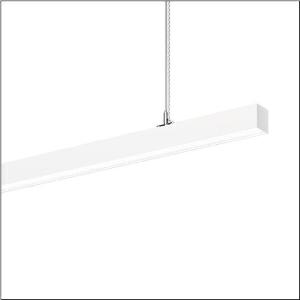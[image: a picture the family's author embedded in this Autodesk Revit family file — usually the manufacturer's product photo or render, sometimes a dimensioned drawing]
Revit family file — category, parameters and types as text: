
# Revit family: silica_r__21_51mx30dc49wb_27b8
name_source: partatom
category: Lighting Fixtures
units: mm (PartAtom-declared; Revit-internal decimal feet)

## family parameters
Cut with Voids When Loaded = No
Host = Face
Light Source = No
Part Type = Normal
Room Calculation Point = No
Round Connector Dimension = Use Diameter
Shared = No

## types (1)
- --- (1 x LED, 10520 lm, 64.1 W, 4000K)
    Apparent Load = 64 VA
    CIE Flux Codes = 47 79 96 57 100
    Color Rendering = 80
    Color Temperature = 4000K
    Default Elevation = 1800 mm
    Description = Silica® 21, office luminaire, primary optical cover: cover, of PMMA, opal, light emission: direct/indirect distribution, primary light characteristic: symmetric, installation type: suspended mounting, LED, rated luminous flux: 10.520lm, luminous efficacy: 164lm/W, light colour: 840, colour temperature: 4000K, with terminal, 3+2-pole, max. 2.5mm², mains connection: 220..240V, AC, 50/60Hz, rated input power: 64.1W, luminaire housing, of aluminium, traffic white (RAL 9016), length: 3.004mm, width: 53mm, height: 53mm, protection rating (complete): IP20, insulation class (complete): insulation class I (protective earthing), certification: CE, permissible operating ambient temperature: 0..+35°C, standard: EN 50419, packaging unit: 1 piece
    Height = 53 mm
    Lamp = 1 x LED
    Lamp Light Flux = 10520 lm
    Lamp Power = 64.1 W
    Lamp count = 1
    Length = 3004 mm
    Luminous efficacy = 164 lm/W
    Manufacturer = Siteco
    ModVariant = No
    Model = 51MX30DC49WB
    Mounting Place = Ceiling
    Mounting Type = Pendant
    Number of Poles = 1
    OnlyDefault = Yes
    Power Factor = 1
    Product Name = Silica® 21
    Product group = office luminaire | ceiling pendant
    ProductGroupID = 902
    Protection Class = Protection class I
    Protection Degree = IP 20
    RLX_Detail_Level = 1
    RLX_Emergency_Light_Flux = 0 lm
    RLX_Emergency_Type = 0
    RLX_Emergency_Type_DB = No
    RlxData = <blob elided: 21337 chars, md5=f2819c2e>
    Socket = socket
    Standby Power = 0 W
    System Light Flux = 10520 lm
    System Power = 64 W
    Type Comments = factory setting: luminous flux: 100 % | dim-lin: 254 | 218 mA
    Type Image = l_1335916.jpg
    URL = http://relux.com
    VarID = @adj_086279
    Voltage = 0 V
    Weight = 0.00 kg
    Width = 53 mm

## geometry (parser evidence)
native form markers: Blend x4, Sweep x10
no freeform markers — native parametric forms only
